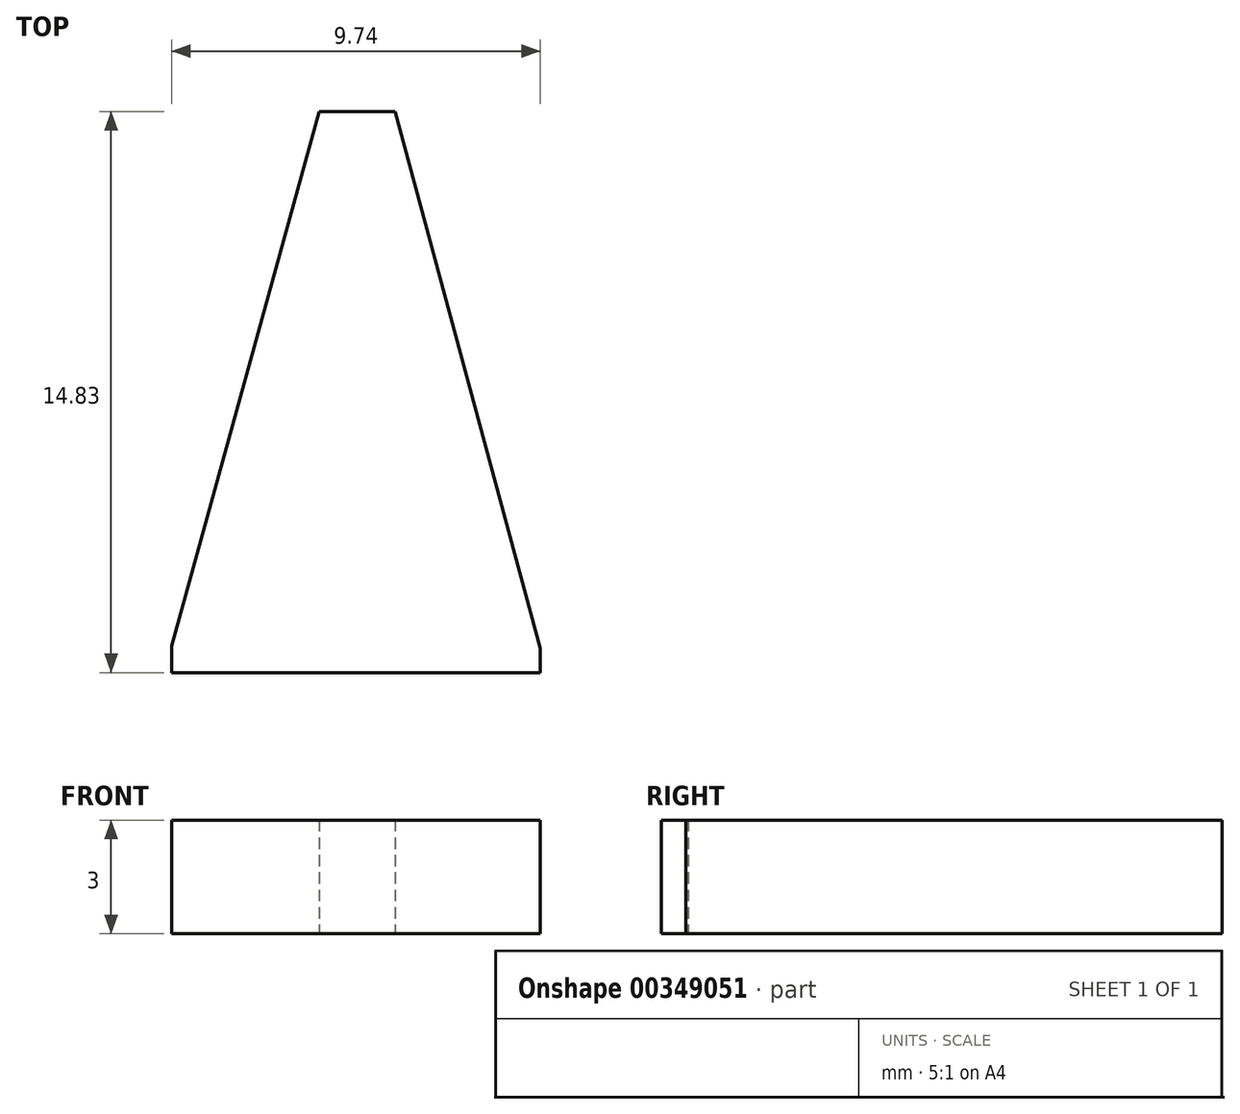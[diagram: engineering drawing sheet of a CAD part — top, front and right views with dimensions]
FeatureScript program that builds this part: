
annotation { "Feature Type Name" : "Feature", "Feature Type Description" : "" }
export const myFeature = defineFeature(function(context is Context, id is Id, definition is map)
    precondition{}
    {
        {
            var Q0;
            Q0=qCreatedBy(makeId("Top.planeOp"),FACE);
            var sketch = newSketch(context, id + "F0", { "sketchPlane" : qUnion([Q0])});
            skLineSegment(sketch, "E0", {"start": v(-34.12, -15.23) * mm, "end": v(-34.12, -14.52) * mm});
            skLineSegment(sketch, "E1", {"start": v(-34.12, -14.52) * mm, "end": v(-30.23, -0.4) * mm});
            skLineSegment(sketch, "E2", {"start": v(-30.23, -0.4) * mm, "end": v(-28.22, -0.4) * mm});
            skLineSegment(sketch, "E3", {"start": v(-28.22, -0.4) * mm, "end": v(-24.38, -14.58) * mm});
            skLineSegment(sketch, "E4", {"start": v(-24.38, -14.58) * mm, "end": v(-24.38, -15.23) * mm});
            skLineSegment(sketch, "E5", {"start": v(-24.38, -15.23) * mm, "end": v(-34.12, -15.23) * mm});
            skSolve(sketch);
        }
        {
            var Q0;
            Q0=makeQuery(id+"F0.imprint","IMPRINT",FACE,{"disambiguationData":[TD([[makeQuery(id+"F0.imprint","IMPRINT",EDGE,{"derivedFrom":sQuery(id+"F0.wireOp",EDGE,"E0")}),-1.0]])]});
            extrude(context, id + "F1", {"entities" : qUnion([Q0]), "depth" : 3 * mm});
        }
    });
